# Revit family: Curtain_Panel_DORMA_ST-Flex-Green_Screenwork_Glass
name_source: partatom
category: Fassadenelemente
revit_build: Autodesk Revit Architecture 2016 (Build: 20150220_1215(x64)
units: mm (PartAtom-declared; Revit-internal decimal feet)

## family parameters
Beim Laden mit Abzugskörper schneiden = Nein
Gemeinsam genutzt = Nein
Immer vertikal = Ja
OmniClass-Nummer = 23.25.20.14.11.11.17
OmniClass-Titel = Infill Panels

## types (1)
- 24mm Double Glazed
    Analytische Konstruktion = <None>
    Barcode = 0
    Glazing Material = Glass-Dorma Glazing-Clear
    NominalHeight = 0
    NominalWidth = 0
    Offset = 0 mm  [stored 0 ft]
    SerialNumber = 0
    TagNumber = 0
    Thickness = 24 mm  [stored 0.0787402 ft]
    WarrentyDuration = 0
    _current revision = 1

note: [stored X ft] marks values corroborated as IEEE doubles in the binary element streams (Revit-internal decimal feet)

## geometry (parser evidence)
native form markers: Sweep x3
no freeform markers — native parametric forms only
